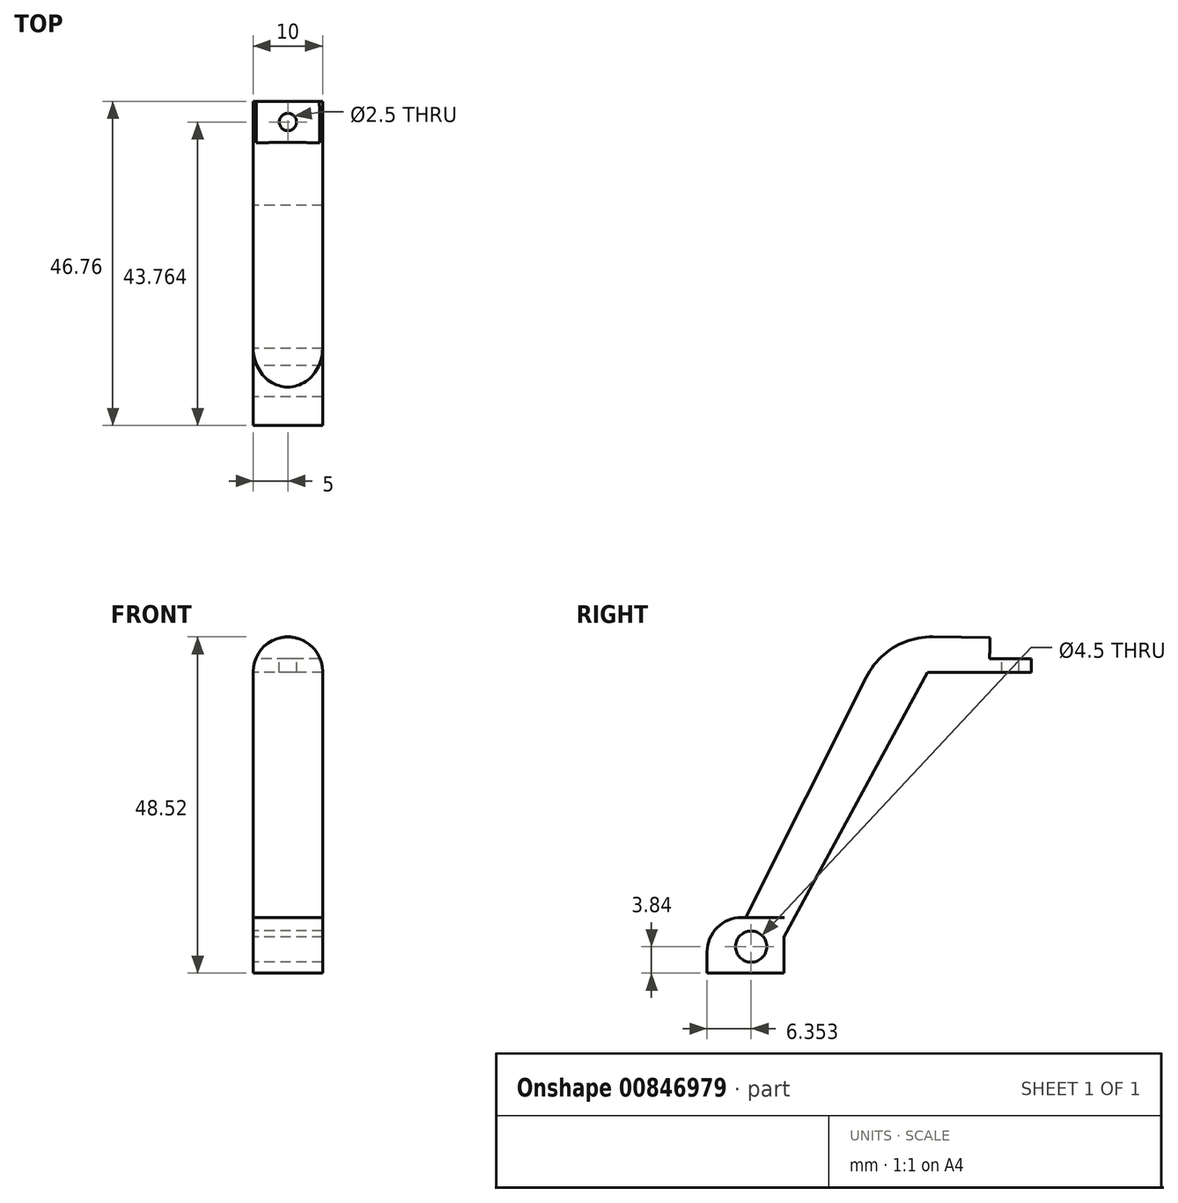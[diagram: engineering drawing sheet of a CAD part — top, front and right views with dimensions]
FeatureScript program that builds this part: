
annotation { "Feature Type Name" : "Feature", "Feature Type Description" : "" }
export const myFeature = defineFeature(function(context is Context, id is Id, definition is map)
    precondition{}
    {
        {
            var Q0;
            Q0=qCreatedBy(makeId("Right.planeOp"),FACE);
            var sketch = newSketch(context, id + "F0", { "sketchPlane" : qUnion([Q0])});
            skLineSegment(sketch, "E0", {"start": v(-22.55, 22.48) * mm, "end": v(-7.55, 22.48) * mm});
            skPoint(sketch, "E1.centerSnap0", {"position": v(-35.57, 0) * mm});
            skCircle(sketch, "E2", {"center": v(-47.96, -17.06) * mm, "radius": 2.25 * mm});
            skLineSegment(sketch, "E3", {"start": v(-28.36, 27.72) * mm, "end": v(-13.5, 27.5) * mm});
            skLineSegment(sketch, "E4", {"start": v(-13.5, 27.5) * mm, "end": v(-13.58, 22.48) * mm});
            skLineSegment(sketch, "E5", {"start": v(-7.55, 22.48) * mm, "end": v(-7.55, 24.5) * mm});
            skLineSegment(sketch, "E6", {"start": v(-7.55, 24.5) * mm, "end": v(-13.55, 24.5) * mm});
            skLineSegment(sketch, "E7.bottom", {"start": v(-54.31, -20.9) * mm, "end": v(-43.22, -20.9) * mm});
            skLineSegment(sketch, "E7.top", {"start": v(-54.31, -12.85) * mm, "end": v(-43.22, -12.85) * mm});
            skLineSegment(sketch, "E7.left", {"start": v(-54.31, -20.9) * mm, "end": v(-54.31, -12.85) * mm});
            skLineSegment(sketch, "E7.right", {"start": v(-43.22, -20.9) * mm, "end": v(-43.22, -12.85) * mm});
            skLineSegment(sketch, "E8", {"start": v(-22.55, 22.48) * mm, "end": v(-43.22, -15.65) * mm});
            skLineSegment(sketch, "E9", {"start": v(-28.36, 27.72) * mm, "end": v(-48.77, -12.85) * mm});
            skSolve(sketch);
        }
        {
            var Q0;
            Q0 = qSketchRegion(id + "F0", true);
            extrude(context, id + "F1", {"entities" : qUnion([Q0]), "depth" : 10 * mm, "offsetDistance" : 25 * mm});
        }
        {
            var Q0;
            Q0=makeQuery(id+"F1.opExtrude","SWEPT_FACE",FACE,{"disambiguationData":[OSD([sQuery(id+"F0.wireOp",EDGE,"E6")])]});
            var sketch = newSketch(context, id + "F2", { "sketchPlane" : qUnion([Q0])});
            skCircle(sketch, "E10", {"center": v(5, -10.55) * mm, "radius": 1 * mm});
            skPoint(sketch, "E10.centerSnap0", {"position": v(0, -10.55) * mm});
            skPoint(sketch, "E10.centerSnap1", {"position": v(5, -7.55) * mm});
            skSolve(sketch);
        }
        {
            var Q0;
            Q0=sQuery(id+"F2.wireOp",VERTEX,"E10.center");
            var Q1;
            Q1=makeQuery(id+"F1.opExtrude","SWEPT_BODY",BODY,{"disambiguationData":[OSD([sQuery(id+"F0.wireOp",EDGE,"E0"),sQuery(id+"F0.wireOp",EDGE,"E2"),sQuery(id+"F0.wireOp",EDGE,"E3"),sQuery(id+"F0.wireOp",EDGE,"E4"),sQuery(id+"F0.wireOp",EDGE,"E5"),sQuery(id+"F0.wireOp",EDGE,"E6"),sQuery(id+"F0.wireOp",EDGE,"E7.bottom"),sQuery(id+"F0.wireOp",EDGE,"E7.top"),sQuery(id+"F0.wireOp",EDGE,"E7.left"),sQuery(id+"F0.wireOp",EDGE,"E7.right"),sQuery(id+"F0.wireOp",EDGE,"E8"),sQuery(id+"F0.wireOp",EDGE,"E9")])]});
            hole(context, id + "F3", {"style" : HoleStyle.SIMPLE, "endStyle" : HoleEndStyle.THROUGH, "holeDiameter" : 2.5 * mm, "majorDiameter" : 5 * mm, "isTappedThrough" : true, "tappedDepth" : 12 * mm, "tapClearance" : 3, "locations" : qUnion([Q0]), "scope" : qUnion([Q1])});
        }
        {
            var Q0;
            Q0=makeQuery(id+"F1.opExtrude","SWEPT_EDGE",EDGE,{"disambiguationData":[OSD([sQuery(id+"F0.wireOp",EDGE,"E3"),sQuery(id+"F0.wireOp",EDGE,"E9")])]});
            fillet(context, id + "F4", {"entities" : qUnion([Q0]), "radius" : 10.54 * mm, "tangentPropagation" : true, "allowEdgeOverflow" : false});
        }
        {
            var Q0;
            Q0=makeQuery(id+"F1.opExtrude","SWEPT_EDGE",EDGE,{"disambiguationData":[OSD([sQuery(id+"F0.wireOp",EDGE,"E7.top"),sQuery(id+"F0.wireOp",EDGE,"E7.left")])]});
            fillet(context, id + "F5", {"entities" : qUnion([Q0]), "radius" : 5 * mm, "tangentPropagation" : true, "allowEdgeOverflow" : false});
        }
        {
            var Q0;
            Q0=makeQuery(id+"F1.opExtrude","CAP_EDGE",EDGE,{"disambiguationData":[OSD([sQuery(id+"F0.wireOp",EDGE,"E9")])],"isStart":false});
            fillet(context, id + "F6", {"entities" : qUnion([Q0]), "radius" : 5 * mm, "tangentPropagation" : true, "allowEdgeOverflow" : false});
        }
        {
            var Q0;
            Q0=makeQuery(id+"F1.opExtrude","CAP_EDGE",EDGE,{"disambiguationData":[OSD([sQuery(id+"F0.wireOp",EDGE,"E9")])],"isStart":true});
            fillet(context, id + "F7", {"entities" : qUnion([Q0]), "radius" : 5 * mm, "tangentPropagation" : true, "allowEdgeOverflow" : false});
        }
    });
